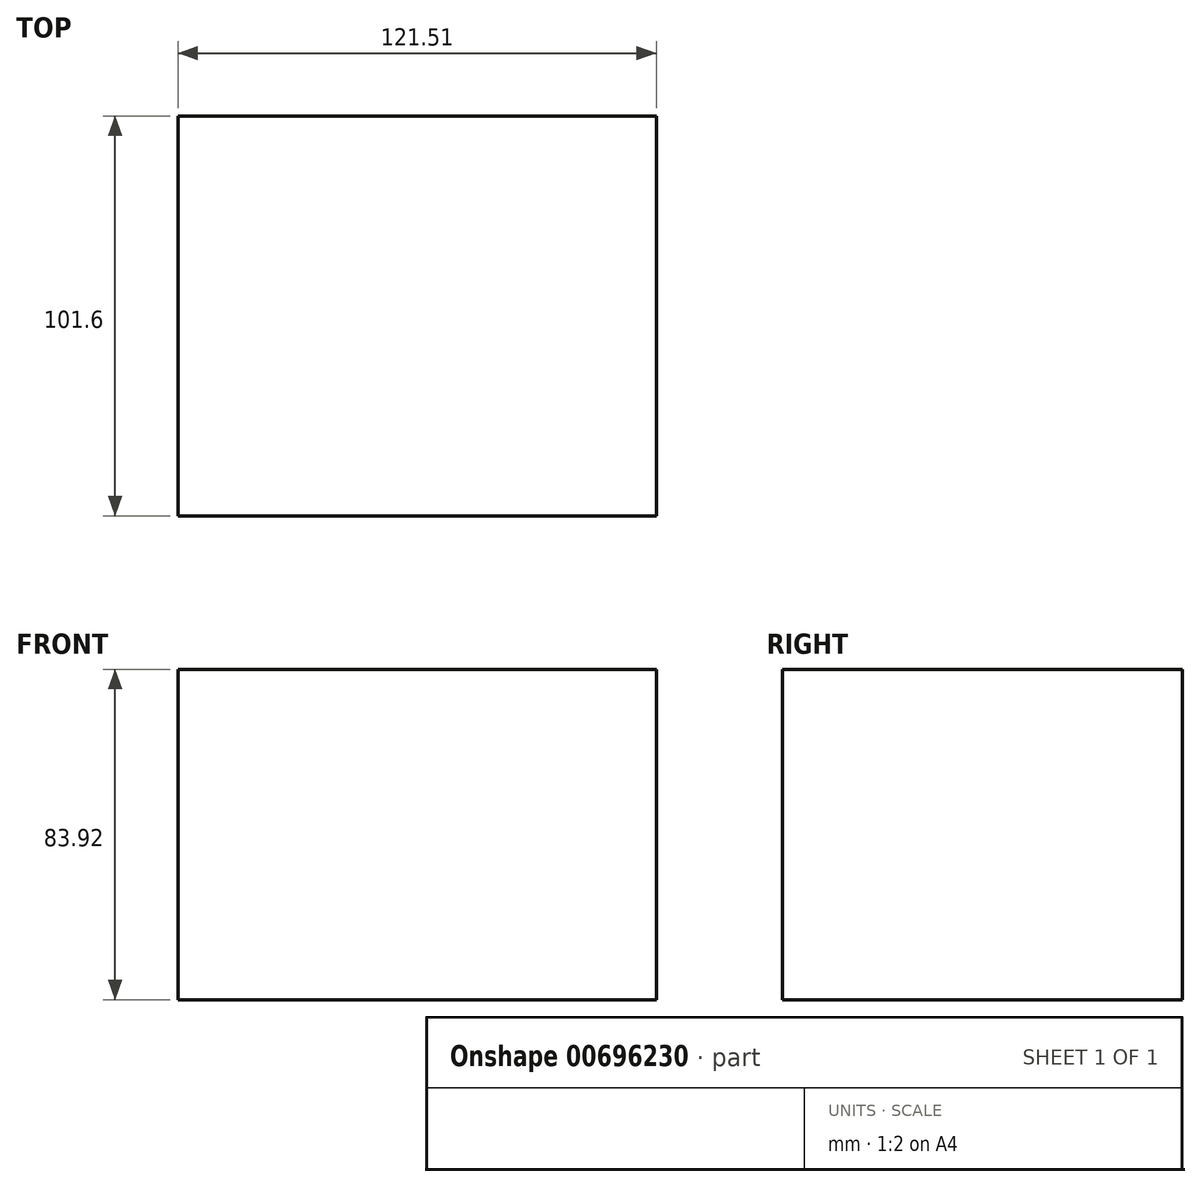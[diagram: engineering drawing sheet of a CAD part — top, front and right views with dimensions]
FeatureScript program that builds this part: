
annotation { "Feature Type Name" : "Feature", "Feature Type Description" : "" }
export const myFeature = defineFeature(function(context is Context, id is Id, definition is map)
    precondition{}
    {
        {
            var Q0;
            Q0=qCreatedBy(makeId("Front.planeOp"),FACE);
            var sketch = newSketch(context, id + "F0", { "sketchPlane" : qUnion([Q0])});
            skLineSegment(sketch, "E0", {"start": v(0, 0) * mm, "end": v(152.4, 0) * mm});
            skLineSegment(sketch, "E1.bottom", {"start": v(-58.8, 38.65) * mm, "end": v(62.71, 38.65) * mm});
            skLineSegment(sketch, "E1.top", {"start": v(-58.8, -45.27) * mm, "end": v(62.71, -45.27) * mm});
            skLineSegment(sketch, "E1.left", {"start": v(-58.8, 38.65) * mm, "end": v(-58.8, -45.27) * mm});
            skLineSegment(sketch, "E1.right", {"start": v(62.71, 38.65) * mm, "end": v(62.71, -45.27) * mm});
            skSolve(sketch);
        }
        {
            var Q0;
            {var subQ0=sQuery(id+"F0.wireOp",EDGE,"E1.bottom");Q0=makeQuery(id+"F0.imprint","IMPRINT",FACE,{"disambiguationData":[TD([[makeQuery(id+"F0.imprint","IMPRINT",EDGE,{"derivedFrom":subQ0}),-1.0]])]});}
            extrude(context, id + "F1", {"entities" : qUnion([Q0]), "depth" : 101.6 * mm, "offsetDistance" : 25.4 * mm});
        }
    });
